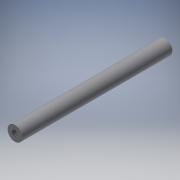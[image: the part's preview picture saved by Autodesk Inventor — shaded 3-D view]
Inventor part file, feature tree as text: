
AUTODESK INVENTOR PART (.ipt)
format: ipt  version: 2017 (Build 210142000, 142)  size: 97,792 bytes
history: native  units: in
note: dims shown in document units (in); Inventor stores cm internally (conversion verified against a paired STEP export)
features: sketch x2, extrude x1, hole x1
ambient origin geometry x8: Origin, YZ Plane, XZ Plane, XY Plane, X Axis, Y Axis, Z Axis, Center Point
bodies: Solid1 (feature_tree)
feature tree (4):
  extrude  "Extrusion1"  Depth=3.568in TaperAngle=0.0deg
  hole  "Hole1"  [1 undecoded]
  sketch  "Sketch1"  dims[d1=0.35in d2=3.568in d3=0.0in]
  sketch  "Sketch2"  dims[d5=0.145in d6=0.38in d7=0.375in d8=0.25in d9=0.5635in d10=0.588in d11=0.8108in]
note: 1 required parameter value undecoded (feature->parameter linkage not recoverable at this tier; creation-order binding heuristic only, values carry confidence <= 0.55)
